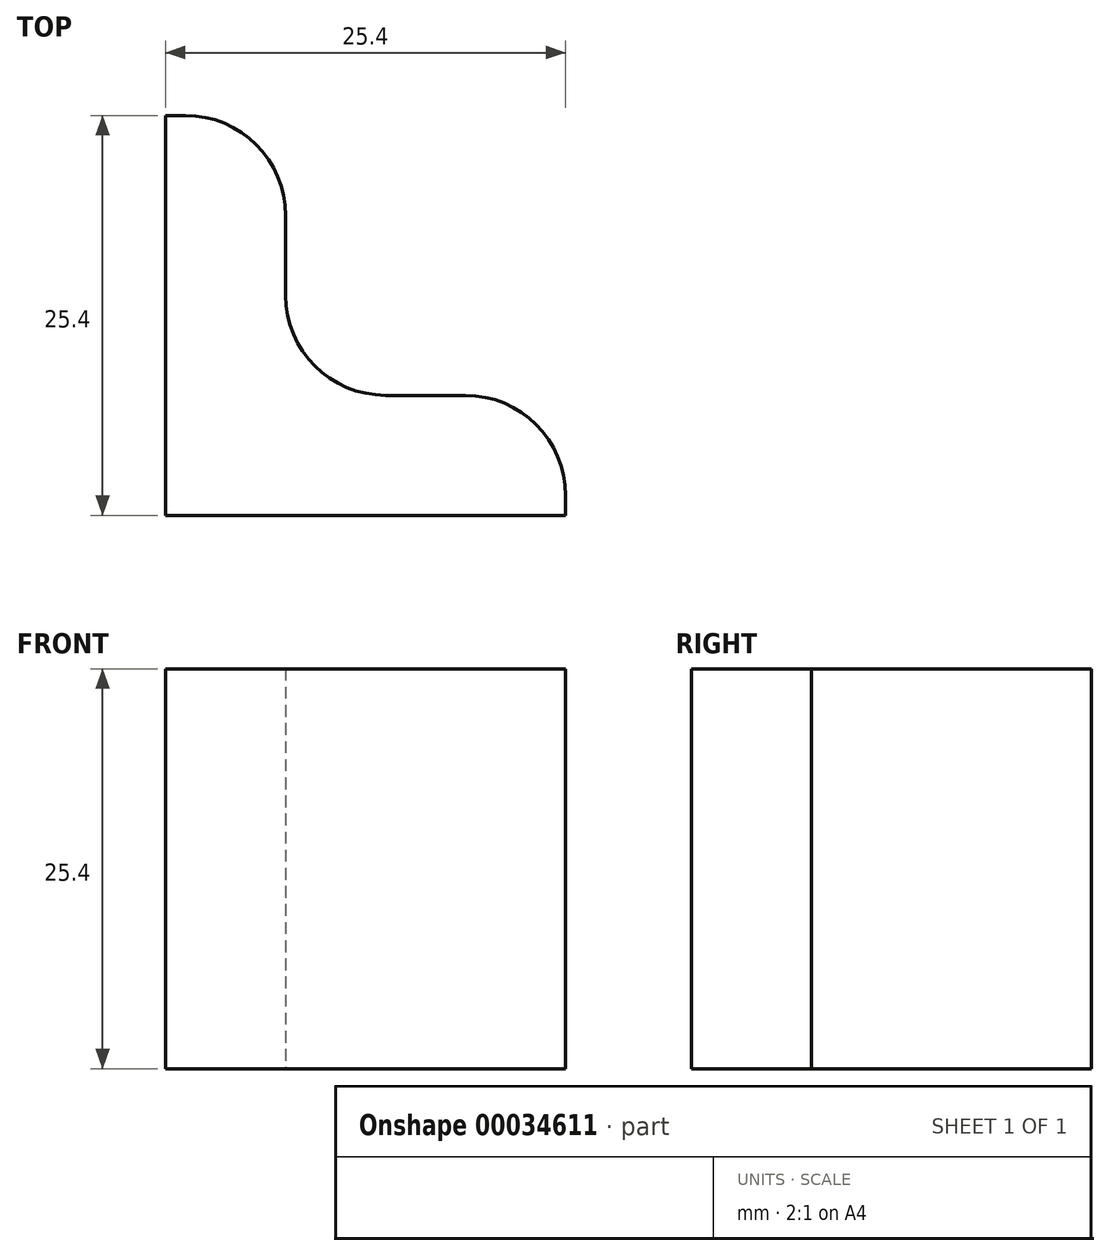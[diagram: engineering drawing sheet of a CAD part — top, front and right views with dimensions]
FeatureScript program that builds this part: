
annotation { "Feature Type Name" : "Feature", "Feature Type Description" : "" }
export const myFeature = defineFeature(function(context is Context, id is Id, definition is map)
    precondition{}
    {
        {
            var Q0;
            Q0=qCreatedBy(makeId("Top.planeOp"),FACE);
            var sketch = newSketch(context, id + "F0", { "sketchPlane" : qUnion([Q0])});
            skLineSegment(sketch, "E0", {"start": v(0, 25.4) * mm, "end": v(0, 0) * mm});
            skLineSegment(sketch, "E1", {"start": v(0, 0) * mm, "end": v(25.4, 0) * mm});
            skLineSegment(sketch, "E2", {"start": v(25.4, 0) * mm, "end": v(25.4, 1.27) * mm});
            skLineSegment(sketch, "E3", {"start": v(19.05, 7.62) * mm, "end": v(13.97, 7.62) * mm});
            skLineSegment(sketch, "E4", {"start": v(7.62, 13.97) * mm, "end": v(7.62, 19.05) * mm});
            skLineSegment(sketch, "E5", {"start": v(1.27, 25.4) * mm, "end": v(0, 25.4) * mm});
            skPoint(sketch, "E6.visualSharp", {"position": v(7.62, 25.4) * mm});
            skArc(sketch, "E6.filletArc", {"start": v(7.62, 19.05) * mm, "mid": v(5.76, 23.54) * mm, "end": v(1.27, 25.4) * mm});
            skPoint(sketch, "E7.visualSharp", {"position": v(25.4, 7.62) * mm});
            skArc(sketch, "E7.filletArc", {"start": v(25.4, 1.27) * mm, "mid": v(23.54, 5.76) * mm, "end": v(19.05, 7.62) * mm});
            skPoint(sketch, "E8.visualSharp", {"position": v(7.62, 7.62) * mm});
            skArc(sketch, "E8.filletArc", {"start": v(7.62, 13.97) * mm, "mid": v(9.48, 9.48) * mm, "end": v(13.97, 7.62) * mm});
            skSolve(sketch);
        }
        {
            var Q0;
            Q0 = qSketchRegion(id + "F0", true);
            extrude(context, id + "F1", {"entities" : qUnion([Q0]), "depth" : 25.4 * mm});
        }
    });
